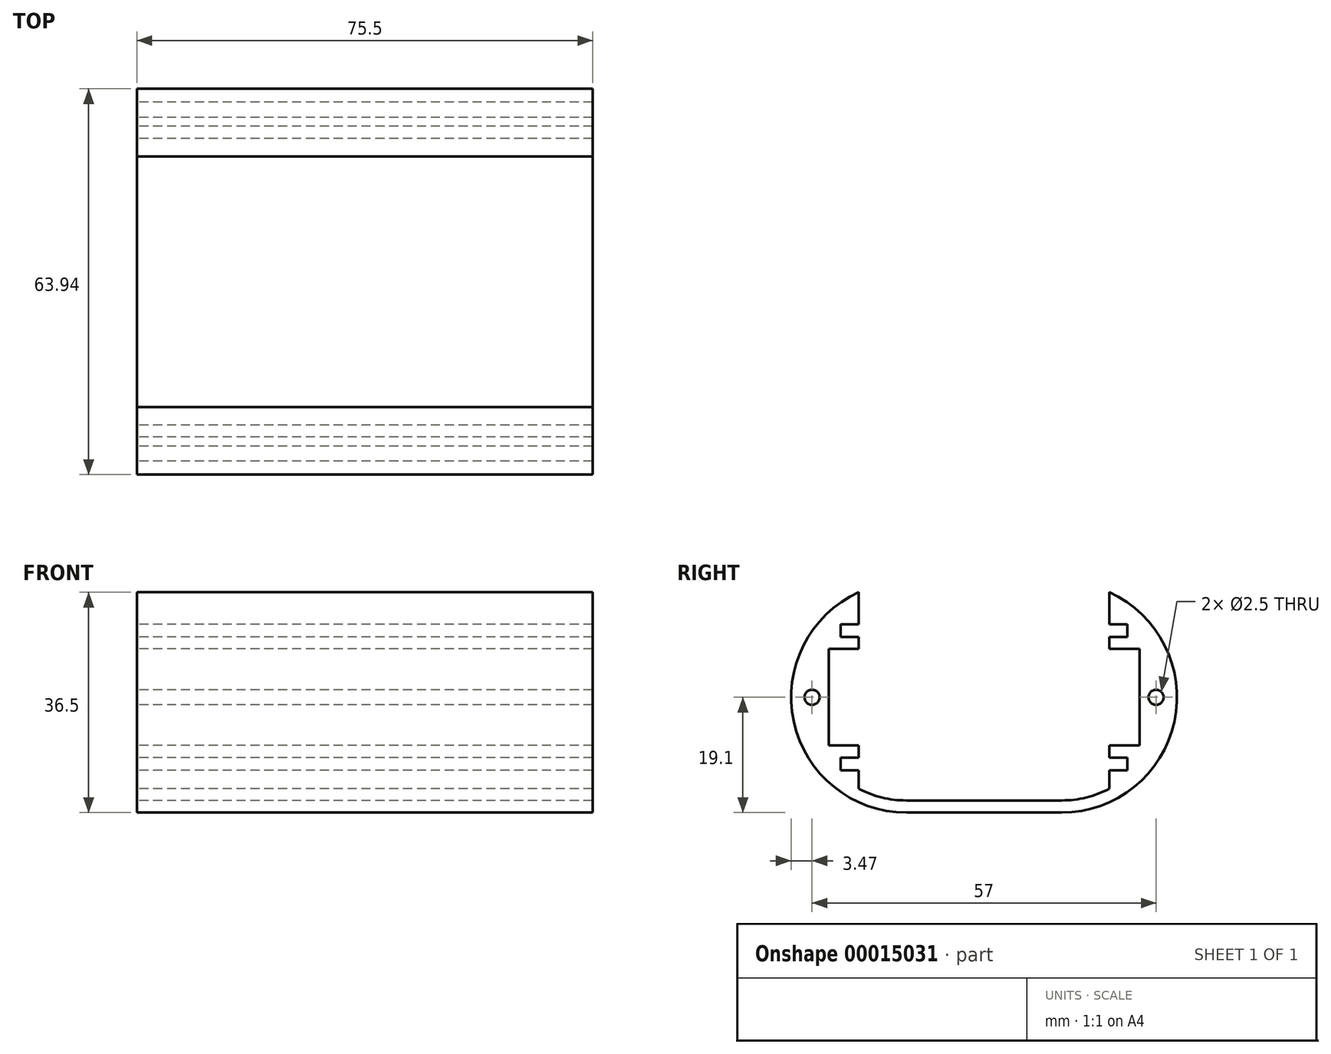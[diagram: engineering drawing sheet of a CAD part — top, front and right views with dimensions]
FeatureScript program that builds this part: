
annotation { "Feature Type Name" : "Feature", "Feature Type Description" : "" }
export const myFeature = defineFeature(function(context is Context, id is Id, definition is map)
    precondition{}
    {
        {
            var Q0;
            Q0=qCreatedBy(makeId("Right.planeOp"),FACE);
            var sketch = newSketch(context, id + "F0", { "sketchPlane" : qUnion([Q0])});
            skLineSegment(sketch, "E0.rect.bottom", {"start": v(23.75, -10) * mm, "end": v(-23.75, -10) * mm});
            skLineSegment(sketch, "E0.rect.top", {"start": v(23.75, 10) * mm, "end": v(-23.75, 10) * mm});
            skLineSegment(sketch, "E0.rect.left", {"start": v(23.75, -10) * mm, "end": v(23.75, 10) * mm});
            skLineSegment(sketch, "E0.rect.right", {"start": v(-23.75, -10) * mm, "end": v(-23.75, 10) * mm});
            skLineSegment(sketch, "E1.bottom", {"start": v(-23.75, 10) * mm, "end": v(23.75, 10) * mm});
            skLineSegment(sketch, "E1.top", {"start": v(-23.75, 12.1) * mm, "end": v(23.75, 12.1) * mm});
            skLineSegment(sketch, "E1.left", {"start": v(-23.75, 10) * mm, "end": v(-23.75, 12.1) * mm});
            skLineSegment(sketch, "E1.right", {"start": v(23.75, 10) * mm, "end": v(23.75, 12.1) * mm});
            skLineSegment(sketch, "E2.bottom", {"start": v(-23.75, -10) * mm, "end": v(23.75, -10) * mm});
            skLineSegment(sketch, "E2.top", {"start": v(-23.75, -12.1) * mm, "end": v(23.75, -12.1) * mm});
            skLineSegment(sketch, "E2.left", {"start": v(-23.75, -10) * mm, "end": v(-23.75, -12.1) * mm});
            skLineSegment(sketch, "E2.right", {"start": v(23.75, -10) * mm, "end": v(23.75, -12.1) * mm});
            skLineSegment(sketch, "E3", {"start": v(-23.75, 10) * mm, "end": v(0, 0) * mm, "construction": true});
            skLineSegment(sketch, "E4", {"start": v(0, 0) * mm, "end": v(23.75, -10) * mm, "construction": true});
            skLineSegment(sketch, "E5", {"start": v(-23.75, -10) * mm, "end": v(-20.75, -10) * mm});
            skLineSegment(sketch, "E6", {"start": v(-20.75, -10) * mm, "end": v(-20.75, -8) * mm});
            skLineSegment(sketch, "E7", {"start": v(-20.75, -8) * mm, "end": v(-25.75, -8) * mm});
            skLineSegment(sketch, "E8", {"start": v(-25.75, -8) * mm, "end": v(-25.75, -14.1) * mm});
            skLineSegment(sketch, "E9", {"start": v(-25.75, -14.1) * mm, "end": v(-20.75, -14.1) * mm});
            skLineSegment(sketch, "E10", {"start": v(-20.75, -14.1) * mm, "end": v(-20.75, -17.1) * mm});
            skLineSegment(sketch, "E11", {"start": v(-20.75, -17.1) * mm, "end": v(20.75, -17.1) * mm});
            skLineSegment(sketch, "E12", {"start": v(20.75, -17.1) * mm, "end": v(20.75, -14.1) * mm});
            skLineSegment(sketch, "E13", {"start": v(20.75, -14.1) * mm, "end": v(25.75, -14.1) * mm});
            skLineSegment(sketch, "E14", {"start": v(25.75, -14.1) * mm, "end": v(25.75, -8) * mm});
            skLineSegment(sketch, "E15", {"start": v(25.75, -8) * mm, "end": v(20.75, -8) * mm});
            skLineSegment(sketch, "E16", {"start": v(20.75, -8) * mm, "end": v(20.75, -10) * mm});
            skLineSegment(sketch, "E17", {"start": v(-20.75, 10) * mm, "end": v(-20.75, 8) * mm});
            skLineSegment(sketch, "E18", {"start": v(-20.75, 8) * mm, "end": v(-25.75, 8) * mm});
            skLineSegment(sketch, "E19", {"start": v(-25.75, 8) * mm, "end": v(-25.75, 14.1) * mm});
            skLineSegment(sketch, "E20", {"start": v(-25.75, 14.1) * mm, "end": v(-20.75, 14.1) * mm});
            skLineSegment(sketch, "E21", {"start": v(-20.75, 14.1) * mm, "end": v(-20.75, 12.1) * mm});
            skLineSegment(sketch, "E22", {"start": v(20.75, 12.1) * mm, "end": v(20.75, 14.1) * mm});
            skLineSegment(sketch, "E23", {"start": v(20.75, 14.1) * mm, "end": v(25.75, 14.1) * mm});
            skLineSegment(sketch, "E24", {"start": v(25.75, 14.1) * mm, "end": v(25.75, 8) * mm});
            skLineSegment(sketch, "E25", {"start": v(25.75, 8) * mm, "end": v(20.75, 8) * mm});
            skLineSegment(sketch, "E26", {"start": v(20.75, 8) * mm, "end": v(20.75, 10) * mm});
            skCircle(sketch, "E27", {"center": v(-28.5, 0) * mm, "radius": 1.25 * mm});
            skCircle(sketch, "E28", {"center": v(28.5, 0) * mm, "radius": 1.25 * mm});
            skLineSegment(sketch, "E29", {"start": v(-28.5, 0) * mm, "end": v(0, 0) * mm, "construction": true});
            skLineSegment(sketch, "E30", {"start": v(28.5, 0) * mm, "end": v(0, 0) * mm, "construction": true});
            skLineSegment(sketch, "E31.bottom", {"start": v(-25.75, -14.1) * mm, "end": v(25.75, -14.1) * mm});
            skLineSegment(sketch, "E31.top", {"start": v(-25.75, -19.1) * mm, "end": v(25.75, -19.1) * mm});
            skLineSegment(sketch, "E31.left", {"start": v(-25.75, -14.1) * mm, "end": v(-25.75, -19.1) * mm});
            skLineSegment(sketch, "E31.right", {"start": v(25.75, -14.1) * mm, "end": v(25.75, -19.1) * mm});
            skArc(sketch, "E32", {"start": v(-12.87, 19.1) * mm, "mid": v(-31.97, 0) * mm, "end": v(-12.87, -19.1) * mm});
            skArc(sketch, "E33", {"start": v(12.87, -19.1) * mm, "mid": v(31.97, 0) * mm, "end": v(12.87, 19.1) * mm});
            skLineSegment(sketch, "E34", {"start": v(-12.87, 19.1) * mm, "end": v(-12.87, 0) * mm, "construction": true});
            skLineSegment(sketch, "E35", {"start": v(-12.87, -19.1) * mm, "end": v(-12.87, 0) * mm, "construction": true});
            skLineSegment(sketch, "E36", {"start": v(12.87, 0) * mm, "end": v(12.87, 19.1) * mm, "construction": true});
            skLineSegment(sketch, "E37", {"start": v(12.87, 0) * mm, "end": v(12.87, -19.1) * mm, "construction": true});
            skLineSegment(sketch, "E38.rect.bottom", {"start": v(24.5, -9.5) * mm, "end": v(11.5, -9.5) * mm});
            skLineSegment(sketch, "E38.rect.top", {"start": v(24.5, 9.5) * mm, "end": v(11.5, 9.5) * mm});
            skLineSegment(sketch, "E38.rect.left", {"start": v(24.5, -9.5) * mm, "end": v(24.5, 9.5) * mm});
            skLineSegment(sketch, "E38.rect.right", {"start": v(11.5, -9.5) * mm, "end": v(11.5, 9.5) * mm});
            skPoint(sketch, "E38.rect.middle", {"position": v(18, 0) * mm});
            skLineSegment(sketch, "E39.rect.bottom", {"start": v(3.75, -7.75) * mm, "end": v(-18.75, -7.75) * mm});
            skLineSegment(sketch, "E39.rect.top", {"start": v(3.75, 7.75) * mm, "end": v(-18.75, 7.75) * mm});
            skLineSegment(sketch, "E39.rect.left", {"start": v(3.75, -7.75) * mm, "end": v(3.75, 7.75) * mm});
            skLineSegment(sketch, "E39.rect.right", {"start": v(-18.75, -7.75) * mm, "end": v(-18.75, 7.75) * mm});
            skPoint(sketch, "E39.rect.middle", {"position": v(-7.5, 0) * mm});
            skCircle(sketch, "E40", {"center": v(-22.25, 0) * mm, "radius": 1.75 * mm});
            skCircle(sketch, "E41", {"center": v(7.25, 0) * mm, "radius": 1.75 * mm});
            skLineSegment(sketch, "E42", {"start": v(-22.25, 0) * mm, "end": v(-7.5, 0) * mm, "construction": true});
            skLineSegment(sketch, "E43", {"start": v(-7.5, 0) * mm, "end": v(7.25, 0) * mm, "construction": true});
            skLineSegment(sketch, "E44.rect.bottom", {"start": v(10.5, 8.5) * mm, "end": v(-25.5, 8.5) * mm});
            skLineSegment(sketch, "E44.rect.top", {"start": v(10.5, -8.5) * mm, "end": v(-25.5, -8.5) * mm});
            skLineSegment(sketch, "E44.rect.left", {"start": v(10.5, 8.5) * mm, "end": v(10.5, -8.5) * mm});
            skLineSegment(sketch, "E44.rect.right", {"start": v(-25.5, 8.5) * mm, "end": v(-25.5, -8.5) * mm});
            skLineSegment(sketch, "E45.rect.bottom", {"start": v(25.5, 10.5) * mm, "end": v(10.5, 10.5) * mm});
            skLineSegment(sketch, "E45.rect.top", {"start": v(25.5, -10.5) * mm, "end": v(10.5, -10.5) * mm});
            skLineSegment(sketch, "E45.rect.left", {"start": v(25.5, 10.5) * mm, "end": v(25.5, -10.5) * mm});
            skLineSegment(sketch, "E45.rect.right", {"start": v(10.5, 10.5) * mm, "end": v(10.5, -10.5) * mm});
            skLineSegment(sketch, "E46", {"start": v(-20.75, 14.1) * mm, "end": v(-20.75, 17.4) * mm});
            skLineSegment(sketch, "E47", {"start": v(20.75, 14.1) * mm, "end": v(20.75, 17.4) * mm});
            skSolve(sketch);
        }
        {
            var Q0;
            Q0=qCreatedBy(makeId("Right.planeOp"),FACE);
            var sketch = newSketch(context, id + "F1", { "sketchPlane" : qUnion([Q0])});
            skArc(sketch, "E48.0", {"start": v(-20.75, 17.4) * mm, "mid": v(-31.54, -4.03) * mm, "end": v(-12.87, -19.1) * mm});
            skArc(sketch, "E48.1", {"start": v(12.87, -19.1) * mm, "mid": v(31.54, -4.03) * mm, "end": v(20.75, 17.4) * mm});
            skLineSegment(sketch, "E49", {"start": v(-20.75, 17.4) * mm, "end": v(-20.75, 12.1) * mm});
            skLineSegment(sketch, "E50", {"start": v(-20.75, 12.1) * mm, "end": v(-23.75, 12.1) * mm});
            skLineSegment(sketch, "E51", {"start": v(-23.75, 12.1) * mm, "end": v(-23.75, 10) * mm});
            skLineSegment(sketch, "E52", {"start": v(-23.75, 10) * mm, "end": v(-20.75, 10) * mm});
            skLineSegment(sketch, "E53", {"start": v(-20.75, 10) * mm, "end": v(-20.75, 8) * mm});
            skLineSegment(sketch, "E54", {"start": v(-20.75, 8) * mm, "end": v(-25.75, 8) * mm});
            skLineSegment(sketch, "E55", {"start": v(-25.75, 8) * mm, "end": v(-25.75, -8) * mm});
            skLineSegment(sketch, "E56", {"start": v(-25.75, -8) * mm, "end": v(-20.75, -8) * mm});
            skLineSegment(sketch, "E57", {"start": v(-20.75, -8) * mm, "end": v(-20.75, -10) * mm});
            skPoint(sketch, "E58.end.orphan", {"position": v(-23.75, -12.1) * mm});
            skLineSegment(sketch, "E59", {"start": v(-20.75, -10) * mm, "end": v(-23.75, -10) * mm});
            skLineSegment(sketch, "E60", {"start": v(-23.75, -10) * mm, "end": v(-23.75, -12.1) * mm});
            skLineSegment(sketch, "E61", {"start": v(-23.75, -12.1) * mm, "end": v(-20.75, -12.1) * mm});
            skLineSegment(sketch, "E62", {"start": v(-20.75, -12.1) * mm, "end": v(-20.75, -14.1) * mm});
            skLineSegment(sketch, "E63.MirrorCS", {"start": v(20.75, -12.1) * mm, "end": v(20.75, -14.1) * mm});
            skLineSegment(sketch, "E64.MirrorCS", {"start": v(20.75, -10) * mm, "end": v(23.75, -10) * mm});
            skLineSegment(sketch, "E65.MirrorCS", {"start": v(23.75, -10) * mm, "end": v(23.75, -12.1) * mm});
            skLineSegment(sketch, "E66.MirrorCS", {"start": v(23.75, 10) * mm, "end": v(20.75, 10) * mm});
            skLineSegment(sketch, "E67.MirrorCS", {"start": v(23.75, 12.1) * mm, "end": v(23.75, 10) * mm});
            skLineSegment(sketch, "E68.MirrorCS", {"start": v(20.75, 12.1) * mm, "end": v(23.75, 12.1) * mm});
            skLineSegment(sketch, "E69.MirrorCS", {"start": v(23.75, -12.1) * mm, "end": v(20.75, -12.1) * mm});
            skLineSegment(sketch, "E70.MirrorCS", {"start": v(20.75, 10) * mm, "end": v(20.75, 8) * mm});
            skLineSegment(sketch, "E71.MirrorCS", {"start": v(20.75, 17.4) * mm, "end": v(20.75, 12.1) * mm});
            skLineSegment(sketch, "E72.MirrorCS", {"start": v(20.75, -8) * mm, "end": v(20.75, -10) * mm});
            skLineSegment(sketch, "E73.MirrorCS", {"start": v(20.75, 8) * mm, "end": v(25.75, 8) * mm});
            skLineSegment(sketch, "E74.MirrorCS", {"start": v(25.75, -8) * mm, "end": v(20.75, -8) * mm});
            skLineSegment(sketch, "E75.MirrorCS", {"start": v(25.75, 8) * mm, "end": v(25.75, -8) * mm});
            skPoint(sketch, "E76.MirrorP", {"position": v(23.75, -12.1) * mm});
            skPoint(sketch, "E77.orphan", {"position": v(-12.87, 19.1) * mm});
            skPoint(sketch, "E78.orphan", {"position": v(12.87, 19.1) * mm});
            skCircle(sketch, "E79.0", {"center": v(-28.5, 0) * mm, "radius": 1.25 * mm});
            skCircle(sketch, "E79.1", {"center": v(28.5, 0) * mm, "radius": 1.25 * mm});
            skLineSegment(sketch, "E80", {"start": v(-12.87, -19.1) * mm, "end": v(12.87, -19.1) * mm});
            skLineSegment(sketch, "E81", {"start": v(-20.75, -14.1) * mm, "end": v(-20.75, -15.17) * mm});
            skArc(sketch, "E82.trimOffspring", {"start": v(-20.75, -15.17) * mm, "mid": v(-16.92, -16.61) * mm, "end": v(-12.87, -17.1) * mm});
            skLineSegment(sketch, "E83", {"start": v(-12.87, -17.1) * mm, "end": v(12.87, -17.1) * mm});
            skLineSegment(sketch, "E84", {"start": v(20.75, -14.1) * mm, "end": v(20.75, -15.17) * mm});
            skArc(sketch, "E85", {"start": v(12.87, -17.1) * mm, "mid": v(16.92, -16.61) * mm, "end": v(20.75, -15.17) * mm});
            skSolve(sketch);
        }
        {
            var Q0;
            Q0 = qSketchRegion(id + "F1", true);
            extrude(context, id + "F2", {"entities" : qUnion([Q0]), "depth" : 75.5 * mm});
        }
    });
